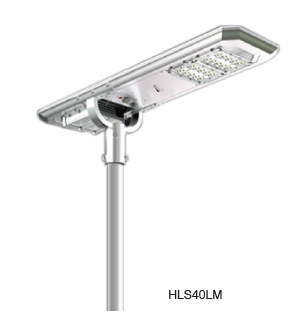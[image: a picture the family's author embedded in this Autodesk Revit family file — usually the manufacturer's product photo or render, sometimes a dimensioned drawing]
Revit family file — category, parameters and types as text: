
# Revit family: HLS40LM
name_source: partatom
category: Lighting Fixtures
units: mm (PartAtom-declared; Revit-internal decimal feet)

## family parameters
Cut with Voids When Loaded = No
Host = Face
Light Source = Yes
Maintain Annotation Orientation = No
Part Type = Normal
Room Calculation Point = No
Round Connector Dimension = Use Diameter
Shared = No

## types (1)
- HLS40LM
    Color Filter = 16777215
    Default Elevation = 1219.20 mm
    Dimming Lamp Color Temperature Shift = <None>
    Emit from Line Length = 609.60 mm
    Keynote = LUCE SOLARE
    Lamp = LED
    Manufacturer = BEGHELLI
    Model = HLS40LM
    POLE HEIGHT = 1550.00 mm
    POLE MATERIAL = BRACKET
    Photometric Web File = HLS40LM.IES
    Tilt Angle = 60.00°
    Type Comments = El luminario Helios de la familia PLANET SUN, integra el
panel fotovoltáico, módulos LED y batería de Li-ion. Es de bajo
mantenimiento, con alta salida de lúmenes y mayor ahorro de
energía. Incluye 3 modos o escenas de iluminación. Incluye
soporte y kit para sujeción de luminario.
    Type Image = HLS40LM (BLS-4A) IMAGE.PNG
    Wattage Comments = 21

## geometry (parser evidence)
native form markers: Sweep x13
no freeform markers — native parametric forms only
